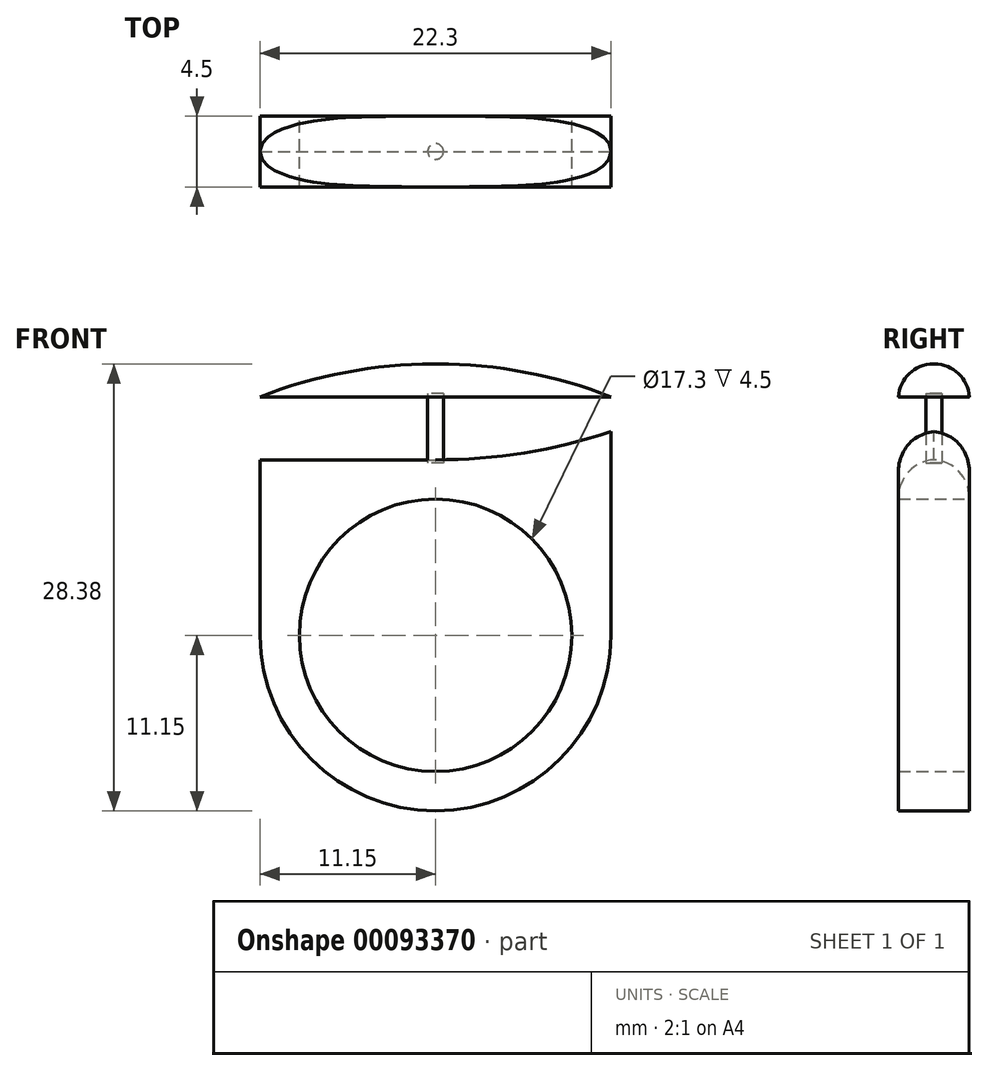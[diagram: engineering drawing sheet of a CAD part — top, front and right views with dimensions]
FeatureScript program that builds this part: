
annotation { "Feature Type Name" : "Feature", "Feature Type Description" : "" }
export const myFeature = defineFeature(function(context is Context, id is Id, definition is map)
    precondition{}
    {
        {
            var Q0;
            Q0=qCreatedBy(makeId("Front.planeOp"),FACE);
            var sketch = newSketch(context, id + "F0", { "sketchPlane" : qUnion([Q0])});
            skCircle(sketch, "E0", {"center": v(0, 0) * mm, "radius": 8.65 * mm});
            skCircle(sketch, "E1.0", {"center": v(0, 0) * mm, "radius": 11.15 * mm});
            skPoint(sketch, "E2", {"position": v(0, 11.15) * mm});
            skPoint(sketch, "E3", {"position": v(11.15, 0) * mm});
            skPoint(sketch, "E4", {"position": v(-11.15, 0) * mm});
            skLineSegment(sketch, "E5", {"start": v(11.15, 0) * mm, "end": v(11.15, 11.15) * mm});
            skLineSegment(sketch, "E6", {"start": v(11.15, 11.15) * mm, "end": v(0, 11.15) * mm});
            skLineSegment(sketch, "E7.MirrorCS", {"start": v(-11.15, 11.15) * mm, "end": v(0, 11.15) * mm});
            skLineSegment(sketch, "E8.MirrorCS", {"start": v(-11.15, 0) * mm, "end": v(-11.15, 11.15) * mm});
            skLineSegment(sketch, "E9", {"start": v(0, 11.15) * mm, "end": v(0, 13.15) * mm, "construction": true});
            skArc(sketch, "E10", {"start": v(0, 11.15) * mm, "mid": v(2, 13.15) * mm, "end": v(0, 15.15) * mm});
            skLineSegment(sketch, "E11", {"start": v(0, 15.15) * mm, "end": v(-11.15, 15.15) * mm});
            skLineSegment(sketch, "E12", {"start": v(-11.15, 15.15) * mm, "end": v(-11.15, 17.23) * mm});
            skLineSegment(sketch, "E13", {"start": v(-11.15, 17.23) * mm, "end": v(11.15, 17.23) * mm});
            skLineSegment(sketch, "E14", {"start": v(11.15, 17.23) * mm, "end": v(11.15, 15.15) * mm});
            skLineSegment(sketch, "E15", {"start": v(11.15, 15.15) * mm, "end": v(0, 15.15) * mm});
            skLineSegment(sketch, "E16", {"start": v(0, 13.15) * mm, "end": v(2, 13.15) * mm});
            skLineSegment(sketch, "E17.MirrorCS", {"start": v(0, 13.15) * mm, "end": v(-2, 13.15) * mm});
            skLineSegment(sketch, "E18", {"start": v(-11.15, 15.15) * mm, "end": v(-11.15, 11.15) * mm, "construction": true});
            skLineSegment(sketch, "E19", {"start": v(-11.15, 13.15) * mm, "end": v(-9.15, 13.15) * mm, "construction": true});
            skArc(sketch, "E20", {"start": v(-9.15, 15.15) * mm, "mid": v(-11.15, 13.15) * mm, "end": v(-9.15, 11.15) * mm});
            skPoint(sketch, "E21", {"position": v(-4, 15.15) * mm});
            skPoint(sketch, "E22", {"position": v(-4, 11.15) * mm});
            skPoint(sketch, "E23", {"position": v(-9.15, 15.15) * mm});
            skPoint(sketch, "E24", {"position": v(-9.15, 11.15) * mm});
            skLineSegment(sketch, "E25", {"start": v(0, 13.15) * mm, "end": v(-4, 13.15) * mm});
            skArc(sketch, "E26", {"start": v(-4, 15.15) * mm, "mid": v(-6, 13.15) * mm, "end": v(-4, 11.15) * mm});
            skArc(sketch, "E27", {"start": v(0, 11.15) * mm, "mid": v(5.65, 11.6) * mm, "end": v(11.15, 12.94) * mm});
            skLineSegment(sketch, "E28", {"start": v(11.15, 12.94) * mm, "end": v(11.15, 11.15) * mm});
            skSolve(sketch);
        }
        {
            var Q0;
            Q0=makeQuery(id+"F0.imprint","IMPRINT",FACE,{"disambiguationData":[TD([[makeQuery(id+"F0.imprint","IMPRINT",EDGE,{"derivedFrom":sQuery(id+"F0.wireOp",EDGE,"E0")}),-1.0]])]});
            var Q1;
            {var subQ0=sQuery(id+"F0.wireOp",EDGE,"E7.MirrorCS");Q1=makeQuery(id+"F0.imprint","IMPRINT",FACE,{"disambiguationData":[TD([[makeQuery(id+"F0.imprint","IMPRINT",EDGE,{"derivedFrom":subQ0}),-1.0]])]});}
            var Q2;
            {var subQ0=sQuery(id+"F0.wireOp",EDGE,"E5");Q2=makeQuery(id+"F0.imprint","IMPRINT",FACE,{"disambiguationData":[TD([[makeQuery(id+"F0.imprint","IMPRINT",EDGE,{"derivedFrom":subQ0}),1.0]])]});}
            var Q3;
            Q3=makeQuery(id+"F0.imprint","IMPRINT",FACE,{"disambiguationData":[TD([[makeQuery(id+"F0.imprint","IMPRINT",EDGE,{"derivedFrom":sQuery(id+"F0.wireOp",EDGE,"E11")}),-1.0]])]});
            var Q4;
            Q4=makeQuery(id+"F0.imprint","IMPRINT",FACE,{"disambiguationData":[TD([[makeQuery(id+"F0.imprint","IMPRINT",EDGE,{"derivedFrom":sQuery(id+"F0.wireOp",EDGE,"E6")}),-1.0]])]});
            extrude(context, id + "F1", {"entities" : qUnion([Q0, Q1, Q2, Q3, Q4]), "depth" : 2.25 * mm, "hasSecondDirection" : true, "secondDirectionOppositeDirection" : true, "secondDirectionDepth" : 2.25 * mm});
        }
        {
            var Q0;
            Q0=makeQuery(id+"F1.opExtrude","SWEPT_FACE",FACE,{"disambiguationData":[OSD([sQuery(id+"F0.wireOp",EDGE,"E6"),sQuery(id+"F0.wireOp",EDGE,"E7.MirrorCS")])]});
            cPlane(context, id + "F2", {"entities" : qUnion([Q0]), "cplaneType" : CPlaneType.OFFSET, "offset" : 2 * mm, "width" : 150 * mm, "height" : 150 * mm});
        }
        {
            var Q0;
            Q0=qCreatedBy(id+"F2.planeOp",FACE);
            var sketch = newSketch(context, id + "F3", { "sketchPlane" : qUnion([Q0])});
            skCircle(sketch, "E29", {"center": v(0, 0) * mm, "radius": 2 * mm});
            skSolve(sketch);
        }
        {
            var Q0;
            Q0=sQuery(id+"F0.wireOp",EDGE,"E10");
            var Q1;
            Q1=sQuery(id+"F3.wireOp",EDGE,"E29");
            revolve(context, id + "F4", {"bodyType" : ToolBodyType.SURFACE, "surfaceEntities" : qUnion([Q0]), "axis" : qUnion([Q1]), "revolveType" : RevolveType.FULL});
        }
        {
            var Q0;
            Q0=makeQuery(id+"F1.opExtrude","SWEPT_EDGE",EDGE,{"disambiguationData":[OSD([sQuery(id+"F0.wireOp",EDGE,"E12"),sQuery(id+"F0.wireOp",EDGE,"E13")])]});
            var Q1;
            Q1=makeQuery(id+"F1.opExtrude","SWEPT_EDGE",EDGE,{"disambiguationData":[OSD([sQuery(id+"F0.wireOp",EDGE,"E13"),sQuery(id+"F0.wireOp",EDGE,"E14")])]});
            fillet(context, id + "F5", {"entities" : qUnion([Q0, Q1]), "radius" : 30.36 * mm, "tangentPropagation" : true, "allowEdgeOverflow" : false});
        }
        {
            var Q0;
            {var subQ0=sQuery(id+"F0.wireOp",EDGE,"E13");var subQ1=sQuery(id+"F0.wireOp",EDGE,"E12");Q0=makeQuery(id+"F5.opFillet","BLEND_EDGE",EDGE,{"blendedFrom":[makeQuery(id+"F1.opExtrude","SWEPT_EDGE",EDGE,{"disambiguationData":[OSD([subQ1,subQ0])]}),makeQuery(id+"F1.opExtrude","CAP_FACE",FACE,{"disambiguationData":[OSD([sQuery(id+"F0.wireOp",EDGE,"E11"),subQ1,subQ0,sQuery(id+"F0.wireOp",EDGE,"E14"),sQuery(id+"F0.wireOp",EDGE,"E15")])],"isStart":false})],"blendedInto":[makeQuery(id+"F1.opExtrude","CAP_FACE",FACE,{"disambiguationData":[OSD([sQuery(id+"F0.wireOp",EDGE,"E11"),subQ1,subQ0,sQuery(id+"F0.wireOp",EDGE,"E14"),sQuery(id+"F0.wireOp",EDGE,"E15")])],"isStart":false})]});}
            var Q1;
            {var subQ0=sQuery(id+"F0.wireOp",EDGE,"E14");var subQ1=sQuery(id+"F0.wireOp",EDGE,"E13");Q1=makeQuery(id+"F5.opFillet","BLEND_EDGE",EDGE,{"blendedFrom":[makeQuery(id+"F1.opExtrude","SWEPT_EDGE",EDGE,{"disambiguationData":[OSD([subQ1,subQ0])]}),makeQuery(id+"F1.opExtrude","CAP_FACE",FACE,{"disambiguationData":[OSD([sQuery(id+"F0.wireOp",EDGE,"E11"),sQuery(id+"F0.wireOp",EDGE,"E12"),subQ1,subQ0,sQuery(id+"F0.wireOp",EDGE,"E15")])],"isStart":true})],"blendedInto":[makeQuery(id+"F1.opExtrude","CAP_FACE",FACE,{"disambiguationData":[OSD([sQuery(id+"F0.wireOp",EDGE,"E11"),sQuery(id+"F0.wireOp",EDGE,"E12"),subQ1,subQ0,sQuery(id+"F0.wireOp",EDGE,"E15")])],"isStart":true})]});}
            fillet(context, id + "F6", {"entities" : qUnion([Q0, Q1]), "radius" : 2.2 * mm, "tangentPropagation" : true, "allowEdgeOverflow" : false});
        }
        {
            var Q0;
            Q0=makeQuery(id+"F1.opExtrude","CAP_EDGE",EDGE,{"disambiguationData":[OSD([sQuery(id+"F0.wireOp",EDGE,"E6"),sQuery(id+"F0.wireOp",EDGE,"E7.MirrorCS")])],"isStart":false});
            var Q1;
            Q1=makeQuery(id+"F1.opExtrude","CAP_EDGE",EDGE,{"disambiguationData":[OSD([sQuery(id+"F0.wireOp",EDGE,"E6"),sQuery(id+"F0.wireOp",EDGE,"E7.MirrorCS")])],"isStart":true});
            fillet(context, id + "F7", {"entities" : qUnion([Q0, Q1]), "radius" : 2.4 * mm, "tangentPropagation" : true, "allowEdgeOverflow" : false});
        }
        {
            var Q0;
            Q0=qCreatedBy(id+"F2.planeOp",FACE);
            var sketch = newSketch(context, id + "F8", { "sketchPlane" : qUnion([Q0])});
            skCircle(sketch, "E30", {"center": v(0, 0) * mm, "radius": 0.5 * mm});
            skSolve(sketch);
        }
        {
            var Q0;
            Q0 = qSketchRegion(id + "F8", true);
            extrude(context, id + "F9", {"entities" : qUnion([Q0]), "depth" : 2.2 * mm, "hasSecondDirection" : true, "secondDirectionOppositeDirection" : true, "secondDirectionDepth" : 2.2 * mm});
        }
    });
